# Revit family: 704330001_Ducha Antivandálica con Regadera Empotrada
name_source: partatom
category: Plumbing Fixtures
units: mm (PartAtom-declared; Revit-internal decimal feet)

## family parameters
Always vertical = Yes
Cut with Voids When Loaded = No
Host = Wall
OmniClass Number = 23.31.11.00
Part Type = Normal
Room Calculation Point = No
Round Connector Dimension = Use Diameter
Shared = No

## types (1)
- Type 1
    Alto = 119 mm
    Alto 2 = 74 mm  [stored 0.242782 ft]
    Altura ducha = 1500 mm  [stored 4.92126 ft]
    Ancho = 320 mm  [stored 1.04987 ft]
    Capacidad de flujo = 6,6L/min - 3,3L /Descarga a 80 Psi.
    Creado por = BIMBAU
    Default Elevation = 0 mm  [stored 0 ft]
    Description = Las duchas Corona son el aliado perfecto para las necesidades de las instituciones de alto tráfico. Diseñadas para un óptimo funcionamiento y durabilidad. Disfruta de sus características antivandálicas y cierre automático temporizado. ¡Pruébala ahora!
    Diametro 2 = 74 mm  [stored 0.242782 ft]
    Diámetro = 55 mm  [stored 0.180446 ft]
    Entrada minimo = 1/2 NPT
    Fecha de creación = 12/03/2021
    Garantía = 3 años
    Manufacturer = Corona
    Material = Corona_Cromo
    Material 2 = Corona_Cobre
    Model = Ducha Antivandálica con Regadera Empotrada
    Peso  Bruto = 799gr. / 1,76Lb.
    Peso neto = 726gr. / 1,60Lb.
    Presión máxima recomendada = 80 Psi.
    Presión mínima recomendada = 20 Psi.
    Profundidad = 273 mm  [stored 0.895669 ft]
    Profundidad 2 = 90 mm
    Referencia = 704330001
    URL = https://corona.co
    Vida útil = 150 Mil Ciclos.

note: [stored X ft] marks values corroborated as IEEE doubles in the binary element streams (Revit-internal decimal feet)

## geometry (parser evidence)
native form markers: Sweep x10
no freeform markers — native parametric forms only
